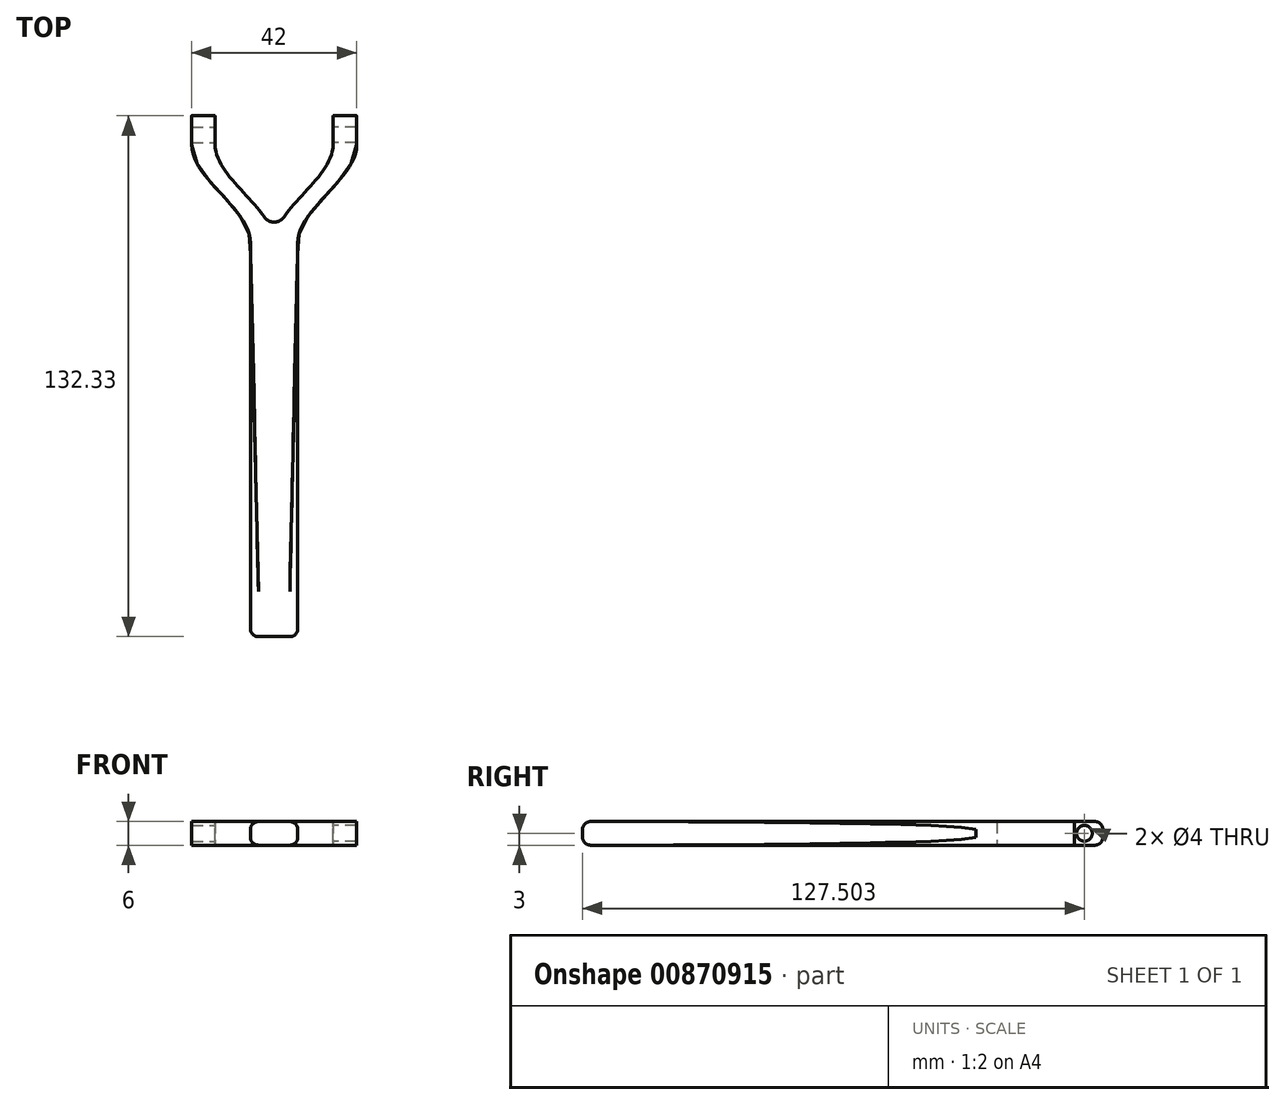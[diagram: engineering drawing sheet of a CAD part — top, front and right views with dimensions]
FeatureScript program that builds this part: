
annotation { "Feature Type Name" : "Feature", "Feature Type Description" : "" }
export const myFeature = defineFeature(function(context is Context, id is Id, definition is map)
    precondition{}
    {
        {
            var Q0;
            Q0=qCreatedBy(makeId("Top.planeOp"),FACE);
            var sketch = newSketch(context, id + "F0", { "sketchPlane" : qUnion([Q0])});
            skLineSegment(sketch, "E0.bottom", {"start": v(-6, 36.54) * mm, "end": v(6, 36.54) * mm});
            skLineSegment(sketch, "E0.top", {"start": v(-6, -63.46) * mm, "end": v(6, -63.46) * mm});
            skLineSegment(sketch, "E0.left", {"start": v(-6, 36.54) * mm, "end": v(-6, -63.46) * mm});
            skLineSegment(sketch, "E0.right", {"start": v(6, 36.54) * mm, "end": v(6, -63.46) * mm});
            skFitSpline(sketch, "E1", {"points": [v(0, 36.54) * mm, v(15, 61.54) * mm], "startDerivative": vector(0.62, 27.49) * mm, "endDerivative": vector(0.62, 27.14) * mm});
            skFitSpline(sketch, "E2", {"points": [v(6, 36.54) * mm, v(21, 61.54) * mm], "startDerivative": vector(0.62, 27.49) * mm, "endDerivative": vector(0.62, 27.14) * mm});
            skLineSegment(sketch, "E3", {"start": v(15, 61.54) * mm, "end": v(21, 61.54) * mm});
            skFitSpline(sketch, "E4.MirrorCS", {"points": [v(0, 36.54) * mm, v(-15, 61.54) * mm], "startDerivative": vector(-0.62, 27.49) * mm, "endDerivative": vector(-0.62, 27.14) * mm});
            skLineSegment(sketch, "E5.MirrorCS", {"start": v(-15, 61.54) * mm, "end": v(-21, 61.54) * mm});
            skFitSpline(sketch, "E6.MirrorCS", {"points": [v(-6, 36.54) * mm, v(-21, 61.54) * mm], "startDerivative": vector(-0.62, 27.49) * mm, "endDerivative": vector(-0.62, 27.14) * mm});
            skSolve(sketch);
        }
        {
            var Q0;
            Q0=makeQuery(id+"F0.imprint","IMPRINT",FACE,{"disambiguationData":[TD([[makeQuery(id+"F0.imprint","IMPRINT",EDGE,{"derivedFrom":sQuery(id+"F0.wireOp",EDGE,"E0.top")}),1.0]])]});
            extrude(context, id + "F1", {"entities" : qUnion([Q0]), "endBound" : BoundingType.SYMMETRIC, "depth" : 6 * mm, "offsetDistance" : 25 * mm});
        }
        {
            var Q0;
            {var subQ2=sQuery(id+"F0.wireOp",EDGE,"E4.MirrorCS");Q0=makeQuery(id+"F0.imprint","IMPRINT",FACE,{"disambiguationData":[TD([[makeQuery(id+"F0.imprint","IMPRINT",EDGE,{"derivedFrom":subQ2}),1.0]])]});}
            var Q1;
            {var subQ2=sQuery(id+"F0.wireOp",EDGE,"E1");Q1=makeQuery(id+"F0.imprint","IMPRINT",FACE,{"disambiguationData":[TD([[makeQuery(id+"F0.imprint","IMPRINT",EDGE,{"derivedFrom":subQ2}),-1.0]])]});}
            extrude(context, id + "F2", {"entities" : qUnion([Q0, Q1]), "operationType" : NewBodyOperationType.ADD, "endBound" : BoundingType.SYMMETRIC, "depth" : 6 * mm, "offsetDistance" : 25 * mm});
        }
        {
            var Q0;
            Q0=makeQuery(id+"F1.opExtrude","CAP_EDGE",EDGE,{"disambiguationData":[OSD([sQuery(id+"F0.wireOp",EDGE,"E0.left")])],"isStart":true});
            var Q1;
            Q1=makeQuery(id+"F1.opExtrude","CAP_EDGE",EDGE,{"disambiguationData":[OSD([sQuery(id+"F0.wireOp",EDGE,"E0.left")])],"isStart":false});
            var Q2;
            Q2=makeQuery(id+"F1.opExtrude","CAP_EDGE",EDGE,{"disambiguationData":[OSD([sQuery(id+"F0.wireOp",EDGE,"E0.right")])],"isStart":true});
            var Q3;
            Q3=makeQuery(id+"F1.opExtrude","CAP_EDGE",EDGE,{"disambiguationData":[OSD([sQuery(id+"F0.wireOp",EDGE,"E0.top")])],"isStart":true});
            var Q4;
            Q4=makeQuery(id+"F1.opExtrude","CAP_EDGE",EDGE,{"disambiguationData":[OSD([sQuery(id+"F0.wireOp",EDGE,"E0.right")])],"isStart":false});
            var Q5;
            Q5=makeQuery(id+"F1.opExtrude","SWEPT_EDGE",EDGE,{"disambiguationData":[OSD([sQuery(id+"F0.wireOp",EDGE,"E0.top"),sQuery(id+"F0.wireOp",EDGE,"E0.right")])]});
            var Q6;
            Q6=makeQuery(id+"F1.opExtrude","SWEPT_FACE",FACE,{"disambiguationData":[OSD([sQuery(id+"F0.wireOp",EDGE,"E0.top")])]});
            var Q7;
            Q7=makeQuery(id+"F1.opExtrude","CAP_EDGE",EDGE,{"disambiguationData":[OSD([sQuery(id+"F0.wireOp",EDGE,"E0.bottom")])],"isStart":true});
            var Q8;
            Q8=makeQuery(id+"F1.opExtrude","CAP_EDGE",EDGE,{"disambiguationData":[OSD([sQuery(id+"F0.wireOp",EDGE,"E0.bottom")])],"isStart":false});
            fillet(context, id + "F3", {"entities" : qUnion([Q0, Q1, Q2, Q3, Q4, Q5, Q6, Q7, Q8]), "radius" : 2 * mm, "tangentPropagation" : true, "allowEdgeOverflow" : false});
        }
        {
            var Q0;
            Q0=qCreatedBy(makeId("Right.planeOp"),FACE);
            cPlane(context, id + "F4", {"entities" : qUnion([Q0]), "cplaneType" : CPlaneType.OFFSET, "offset" : 15 * mm, "width" : 150 * mm, "height" : 150 * mm});
        }
        {
            var Q0;
            Q0=qCreatedBy(id+"F4.planeOp",FACE);
            var sketch = newSketch(context, id + "F5", { "sketchPlane" : qUnion([Q0])});
            skCircle(sketch, "E7", {"center": v(64.04, 0) * mm, "radius": 2 * mm});
            skCircle(sketch, "E8", {"center": v(64.04, 0) * mm, "radius": 4.83 * mm});
            skLineSegment(sketch, "E9", {"start": v(60.26, 3) * mm, "end": v(67.82, 3) * mm});
            skLineSegment(sketch, "E10", {"start": v(60.26, -3) * mm, "end": v(67.82, -3) * mm});
            skLineSegment(sketch, "E11", {"start": v(61.54, -4.13) * mm, "end": v(61.54, 4.13) * mm});
            skSolve(sketch);
        }
        {
            var Q0;
            Q0=makeQuery(id+"F5.imprint","IMPRINT",FACE,{"disambiguationData":[TD([[makeQuery(id+"F5.imprint","IMPRINT",EDGE,{"derivedFrom":sQuery(id+"F5.wireOp",EDGE,"E7")}),-1.0]])]});
            extrude(context, id + "F6", {"entities" : qUnion([Q0]), "operationType" : NewBodyOperationType.ADD, "depth" : 6 * mm, "offsetDistance" : 25 * mm});
        }
        {
            var Q0;
            Q0=makeQuery(id+"F6.opExtrude","SWEPT_EDGE",EDGE,{"disambiguationData":[OSD([sQuery(id+"F5.wireOp",EDGE,"E8"),sQuery(id+"F5.wireOp",EDGE,"E9")])]});
            var Q1;
            Q1=makeQuery(id+"F6.opExtrude","SWEPT_EDGE",EDGE,{"disambiguationData":[OSD([sQuery(id+"F5.wireOp",EDGE,"E8"),sQuery(id+"F5.wireOp",EDGE,"E10")])]});
            fillet(context, id + "F7", {"entities" : qUnion([Q0, Q1]), "radius" : 2 * mm, "tangentPropagation" : true, "allowEdgeOverflow" : false});
        }
        {
            var Q0;
            {var subQ0=sQuery(id+"F0.wireOp",EDGE,"E4.MirrorCS");var subQ1=sQuery(id+"F0.wireOp",EDGE,"E1");var subQ2=sQuery(id+"F0.wireOp",EDGE,"E0.bottom");Q0=makeQuery(id+"F2.boolean.opBoolean","MERGE",EDGE,{"derivedFrom":[makeQuery(id+"F2.opExtrude","SWEPT_EDGE",EDGE,{"disambiguationData":[OSD([subQ2,subQ1,subQ0]),OD(0.0)]}),makeQuery(id+"F2.opExtrude","SWEPT_EDGE",EDGE,{"disambiguationData":[OSD([subQ2,subQ1,subQ0]),OD(1.0)]})]});}
            fillet(context, id + "F8", {"entities" : qUnion([Q0]), "radius" : 3 * mm, "tangentPropagation" : true, "allowEdgeOverflow" : false});
        }
        {
            var Q0;
            Q0=makeQuery(id+"F1.opExtrude","SWEPT_BODY",BODY,{"disambiguationData":[OSD([sQuery(id+"F0.wireOp",EDGE,"E0.bottom"),sQuery(id+"F0.wireOp",EDGE,"E0.top"),sQuery(id+"F0.wireOp",EDGE,"E0.left"),sQuery(id+"F0.wireOp",EDGE,"E0.right")])]});
            var Q1;
            Q1=qCreatedBy(makeId("Right.planeOp"),FACE);
            mirror(context, id + "F9", {"operationType" : NewBodyOperationType.ADD, "entities" : qUnion([Q0]), "mirrorPlane" : qUnion([Q1])});
        }
    });
